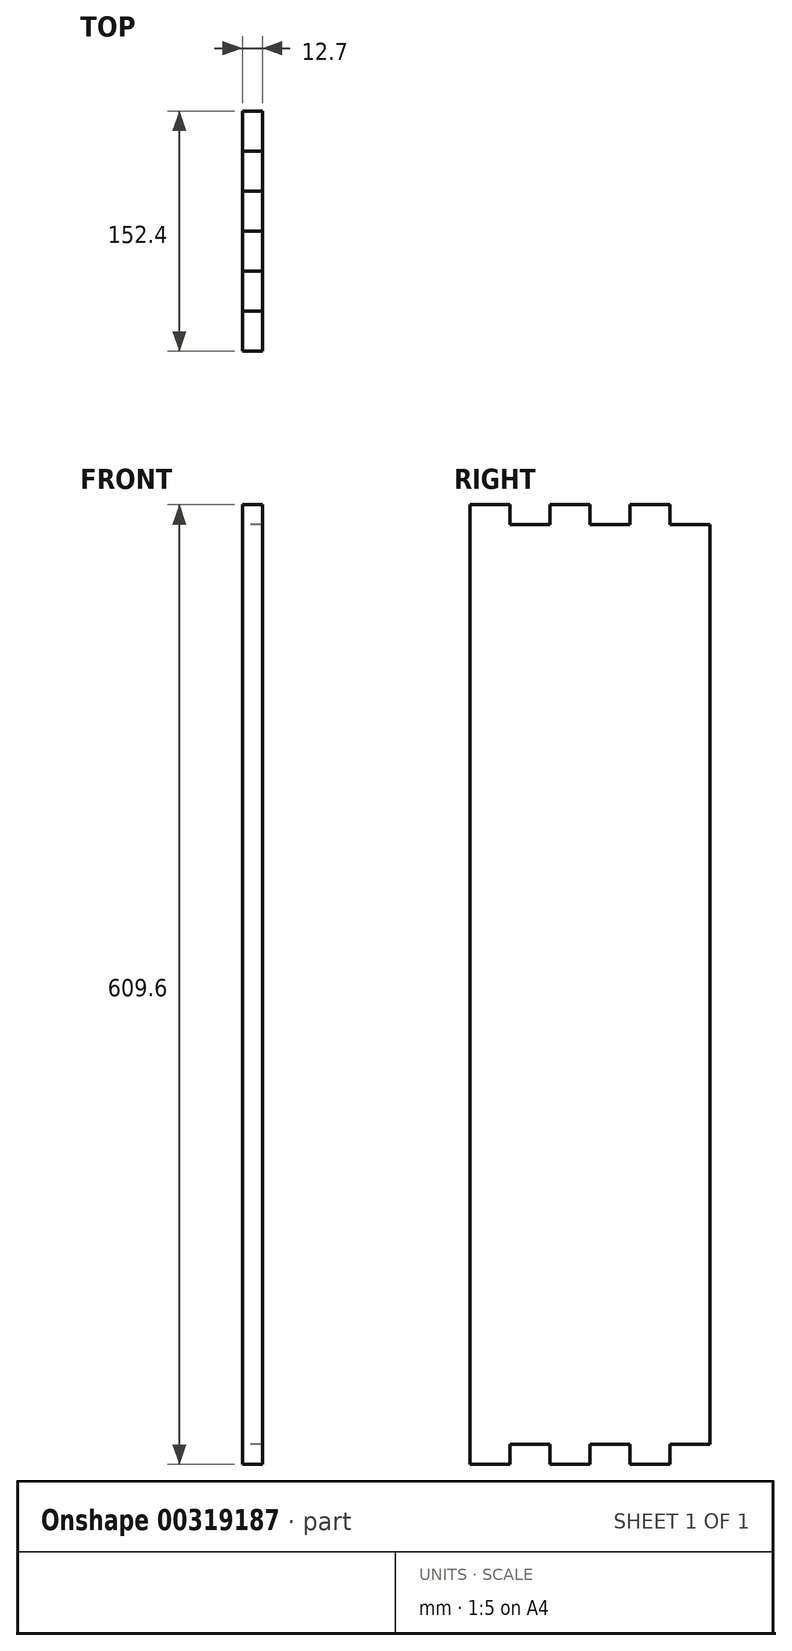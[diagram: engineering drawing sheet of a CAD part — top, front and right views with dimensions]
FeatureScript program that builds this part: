
annotation { "Feature Type Name" : "Feature", "Feature Type Description" : "" }
export const myFeature = defineFeature(function(context is Context, id is Id, definition is map)
    precondition{}
    {
        {
            var Q0;
            Q0=qCreatedBy(makeId("Right.planeOp"),FACE);
            var sketch = newSketch(context, id + "F0", { "sketchPlane" : qUnion([Q0])});
            skLineSegment(sketch, "E0.bottom", {"start": v(76.2, 304.8) * mm, "end": v(-76.2, 304.8) * mm});
            skLineSegment(sketch, "E0.top", {"start": v(76.2, -304.8) * mm, "end": v(-76.2, -304.8) * mm});
            skLineSegment(sketch, "E0.left", {"start": v(76.2, 304.8) * mm, "end": v(76.2, -304.8) * mm});
            skLineSegment(sketch, "E0.right", {"start": v(-76.2, 304.8) * mm, "end": v(-76.2, -304.8) * mm});
            skPoint(sketch, "E0.middle", {"position": v(0, 0) * mm});
            skLineSegment(sketch, "E1.bottom", {"start": v(-50.8, 304.8) * mm, "end": v(-25.4, 304.8) * mm});
            skLineSegment(sketch, "E1.top", {"start": v(-50.8, 292.1) * mm, "end": v(-25.4, 292.1) * mm});
            skLineSegment(sketch, "E1.left", {"start": v(-50.8, 304.8) * mm, "end": v(-50.8, 292.1) * mm});
            skLineSegment(sketch, "E1.right", {"start": v(-25.4, 304.8) * mm, "end": v(-25.4, 292.1) * mm});
            skLineSegment(sketch, "E2.1.0.0", {"start": v(25.4, 304.8) * mm, "end": v(25.4, 292.1) * mm});
            skLineSegment(sketch, "E2.1.0.1", {"start": v(0, 304.8) * mm, "end": v(0, 292.1) * mm});
            skLineSegment(sketch, "E2.1.0.2", {"start": v(0, 292.1) * mm, "end": v(25.4, 292.1) * mm});
            skLineSegment(sketch, "E2.1.0.3", {"start": v(0, 304.8) * mm, "end": v(25.4, 304.8) * mm});
            skLineSegment(sketch, "E2.2.0.0", {"start": v(76.2, 304.8) * mm, "end": v(76.2, 292.1) * mm});
            skLineSegment(sketch, "E2.2.0.1", {"start": v(50.8, 304.8) * mm, "end": v(50.8, 292.1) * mm});
            skLineSegment(sketch, "E2.2.0.2", {"start": v(50.8, 292.1) * mm, "end": v(76.2, 292.1) * mm});
            skLineSegment(sketch, "E2.2.0.3", {"start": v(50.8, 304.8) * mm, "end": v(76.2, 304.8) * mm});
            skLineSegment(sketch, "E2.direction1", {"start": v(-50.8, 292.1) * mm, "end": v(0, 292.1) * mm, "construction": true});
            skLineSegment(sketch, "E3.MirrorCS", {"start": v(50.8, -304.8) * mm, "end": v(76.2, -304.8) * mm});
            skLineSegment(sketch, "E4.MirrorCS", {"start": v(-50.8, -292.1) * mm, "end": v(-25.4, -292.1) * mm});
            skLineSegment(sketch, "E5.MirrorCS", {"start": v(-50.8, -292.1) * mm, "end": v(0, -292.1) * mm, "construction": true});
            skLineSegment(sketch, "E6.MirrorCS", {"start": v(76.2, -304.8) * mm, "end": v(76.2, -292.1) * mm});
            skLineSegment(sketch, "E7.MirrorCS", {"start": v(0, -304.8) * mm, "end": v(25.4, -304.8) * mm});
            skLineSegment(sketch, "E8.MirrorCS", {"start": v(-50.8, -304.8) * mm, "end": v(-25.4, -304.8) * mm});
            skLineSegment(sketch, "E9.MirrorCS", {"start": v(-50.8, -304.8) * mm, "end": v(-50.8, -292.1) * mm});
            skLineSegment(sketch, "E10.MirrorCS", {"start": v(-25.4, -304.8) * mm, "end": v(-25.4, -292.1) * mm});
            skLineSegment(sketch, "E11.MirrorCS", {"start": v(76.2, -304.8) * mm, "end": v(76.2, 304.8) * mm});
            skLineSegment(sketch, "E12.MirrorCS", {"start": v(50.8, -292.1) * mm, "end": v(76.2, -292.1) * mm});
            skLineSegment(sketch, "E13.MirrorCS", {"start": v(0, -292.1) * mm, "end": v(25.4, -292.1) * mm});
            skLineSegment(sketch, "E14.MirrorCS", {"start": v(25.4, -304.8) * mm, "end": v(25.4, -292.1) * mm});
            skLineSegment(sketch, "E15.MirrorCS", {"start": v(50.8, -304.8) * mm, "end": v(50.8, -292.1) * mm});
            skLineSegment(sketch, "E16.MirrorCS", {"start": v(0, -304.8) * mm, "end": v(0, -292.1) * mm});
            skSolve(sketch);
        }
        {
            var Q0;
            {var subQ3=sQuery(id+"F0.wireOp",EDGE,"E0.right");Q0=makeQuery(id+"F0.imprint","IMPRINT",FACE,{"disambiguationData":[TD([[makeQuery(id+"F0.imprint","IMPRINT",EDGE,{"derivedFrom":subQ3}),1.0]])]});}
            extrude(context, id + "F1", {"entities" : qUnion([Q0]), "depth" : 12.7 * mm});
        }
    });
